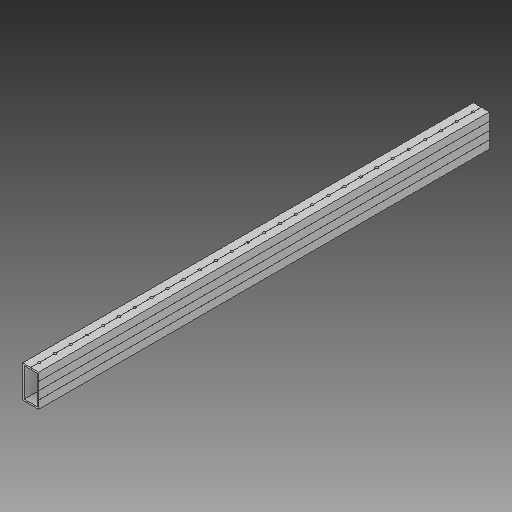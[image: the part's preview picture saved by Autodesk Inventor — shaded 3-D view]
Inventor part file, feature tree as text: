
AUTODESK INVENTOR PART (.ipt)
format: ipt  version: 2017 (Build 210142000, 142)  size: 545,792 bytes
history: native  units: in
note: dims shown in document units (in); Inventor stores cm internally (conversion verified against a paired STEP export)
features: reference x14, other x7, extrude x2, sketch x2, pattern_linear x1
ambient origin geometry x8: Origin, YZ Plane, XZ Plane, XY Plane, X Axis, Y Axis, Z Axis, Center Point
bodies: Solid1 (feature_tree)
feature tree (26):
  extrude  "Extrusion1"  Depth=1.0in TaperAngle=0.0deg
  extrude  "Extrusion4"  Depth=1.0in
  pattern_linear  "Rectangular Pattern2"  Spacing1=1.5in  [1 undecoded]
  sketch  "Sketch1"  dims[d0=28.0in d1=1.0in d2=0.0in]
  reference  "Reference1"
  reference  "Reference2"
  reference  "Reference3"
  reference  "Reference4"
  reference  "Reference5"
  reference  "Reference6"
  reference  "Reference7"
  reference  "Reference8"
  reference  "Reference9"
  reference  "Reference10"
  reference  "Reference11"
  reference  "Reference12"
  reference  "Reference13"
  reference  "Reference14"
  sketch  "Sketch5"  dims[d20=3.5in d21=0.25in d22=1.5in d23=1.5in d24=0.1in d25=0.1in d26=1.0in d27=0.0in d28=5.5118in d30=1.5in]
  other  "Cut-Extrude2"
  parser-record x1  (decoder bookkeeping rows leaked as tree rows — omitted from the tree; the rows remain in map.json)
  other  "2898-17-A-0100.iam"
  other  "SideFrame:1"
  other  "2898-17-P-0101:1"
  other  "VersaChassis_Gusset:1"
  other  "VersaChassis_Gusset:2"
note: 1 required parameter value undecoded (feature->parameter linkage not recoverable at this tier; creation-order binding heuristic only, values carry confidence <= 0.55)
note: 1 file-system path scrubbed to <path> (originals preserved in map.json)
